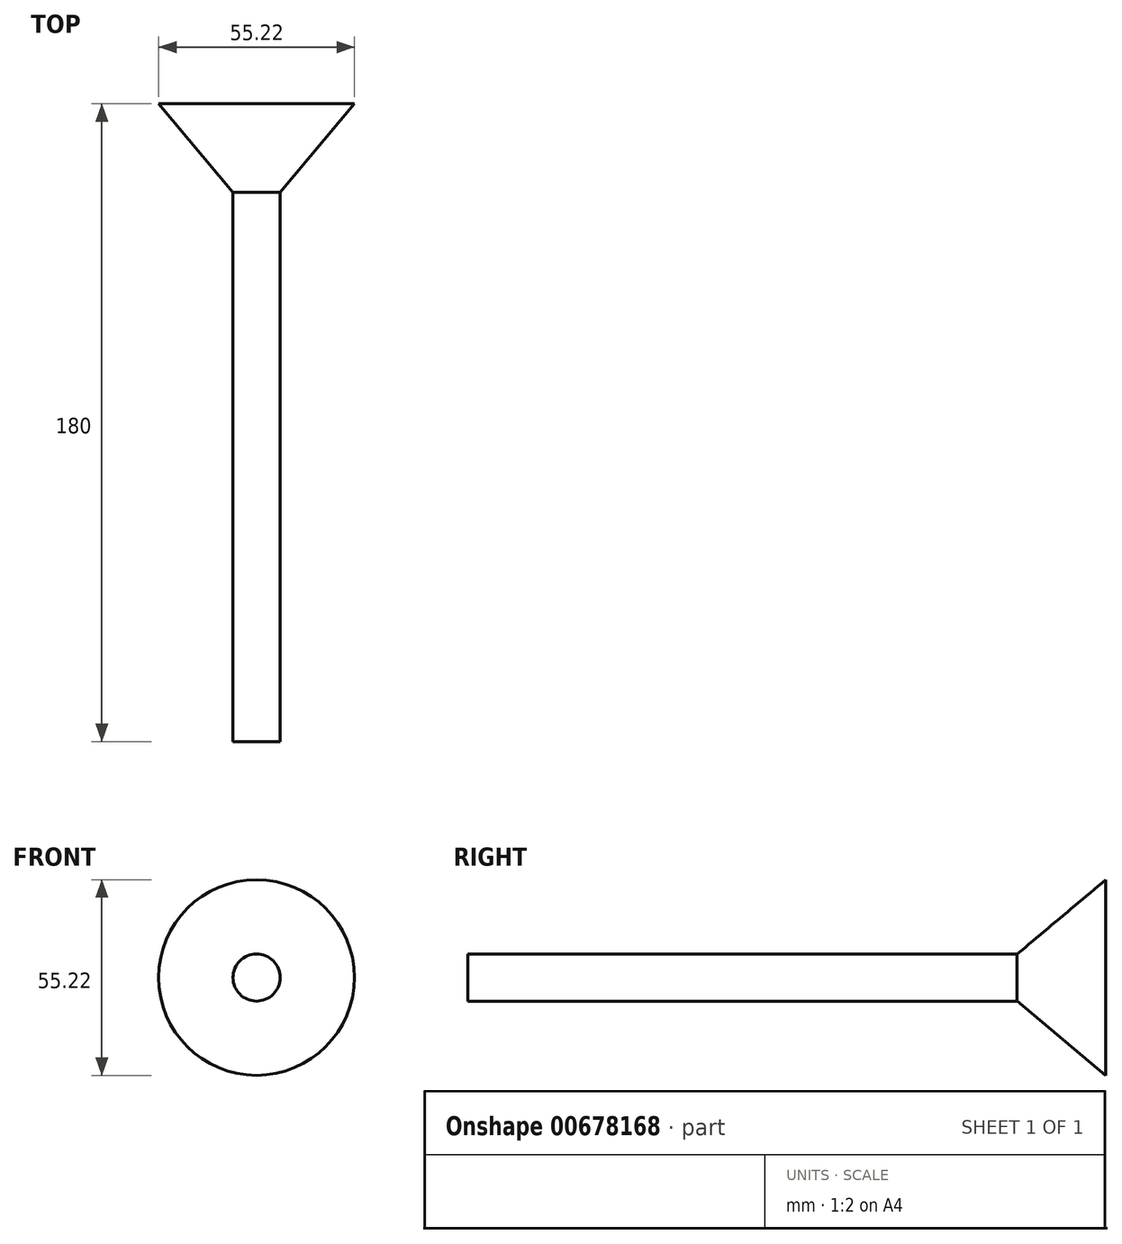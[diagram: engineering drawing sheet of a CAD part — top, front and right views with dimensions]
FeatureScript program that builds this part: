
annotation { "Feature Type Name" : "Feature", "Feature Type Description" : "" }
export const myFeature = defineFeature(function(context is Context, id is Id, definition is map)
    precondition{}
    {
        {
            var Q0;
            Q0=qCreatedBy(makeId("Front.planeOp"),FACE);
            var sketch = newSketch(context, id + "F0", { "sketchPlane" : qUnion([Q0])});
            skCircle(sketch, "E0", {"center": v(0, 0) * mm, "radius": 6.64 * mm});
            skSolve(sketch);
        }
        {
            var Q0;
            Q0=makeQuery(id+"F0.imprint","IMPRINT",FACE,{"disambiguationData":[TD([[makeQuery(id+"F0.imprint","IMPRINT",EDGE,{"derivedFrom":sQuery(id+"F0.wireOp",EDGE,"E0")}),1.0]])]});
            extrude(context, id + "F1", {"entities" : qUnion([Q0]), "depth" : 155 * mm, "offsetDistance" : 25 * mm});
        }
        {
            var Q0;
            Q0=makeQuery(id+"F1.opExtrude","CAP_FACE",FACE,{"disambiguationData":[OSD([sQuery(id+"F0.wireOp",EDGE,"E0")])],"isStart":true});
            var sketch = newSketch(context, id + "F2", { "sketchPlane" : qUnion([Q0])});
            skCircle(sketch, "E1", {"center": v(0, 0) * mm, "radius": 6.63 * mm});
            skSolve(sketch);
        }
        {
            var Q0;
            Q0=makeQuery(id+"F2.imprint","IMPRINT",FACE,{"disambiguationData":[TD([[makeQuery(id+"F2.imprint","IMPRINT",EDGE,{"derivedFrom":sQuery(id+"F2.wireOp",EDGE,"E1")}),1.0]])]});
            extrude(context, id + "F3", {"entities" : qUnion([Q0]), "operationType" : NewBodyOperationType.ADD, "depth" : 25 * mm, "offsetDistance" : 25 * mm, "hasDraft" : true, "draftAngle" : 40 * degree});
        }
    });
